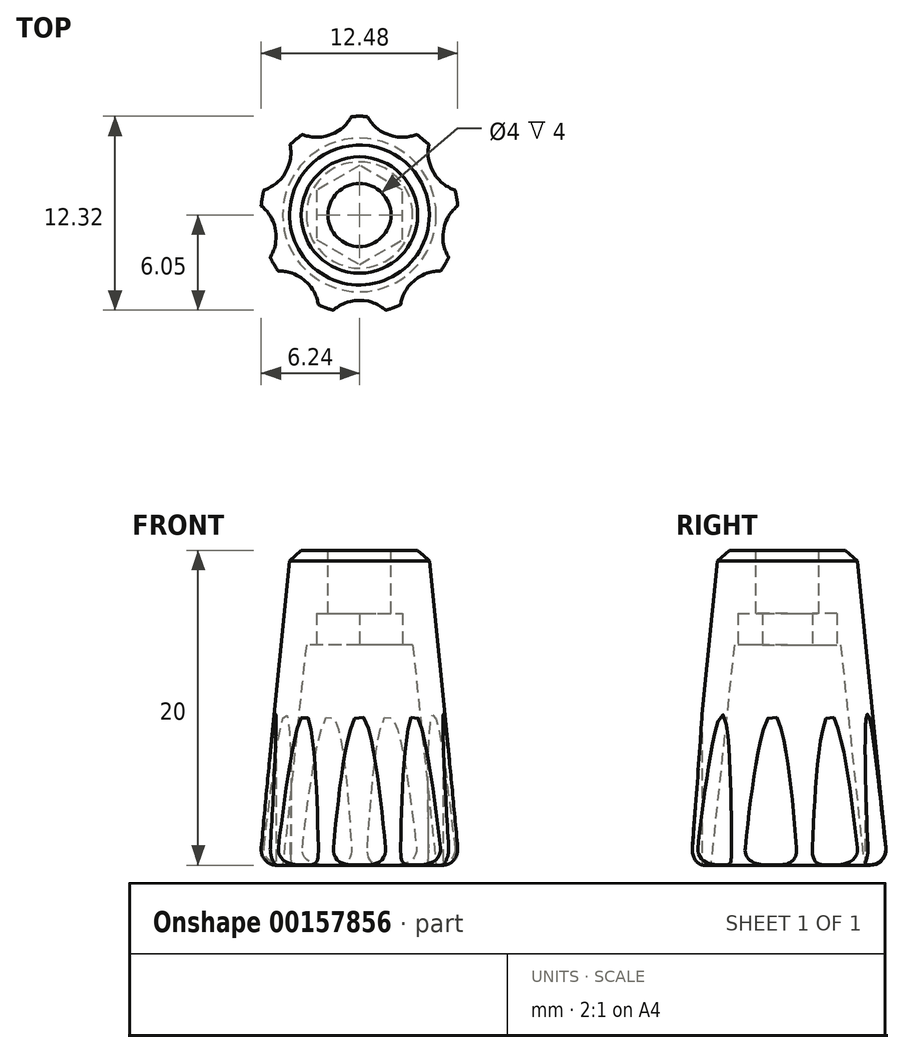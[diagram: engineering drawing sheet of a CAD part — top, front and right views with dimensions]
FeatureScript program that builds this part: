
annotation { "Feature Type Name" : "Feature", "Feature Type Description" : "" }
export const myFeature = defineFeature(function(context is Context, id is Id, definition is map)
    precondition{}
    {
        {
            var Q0;
            Q0=qCreatedBy(makeId("Top.planeOp"),FACE);
            var sketch = newSketch(context, id + "F0", { "sketchPlane" : qUnion([Q0])});
            skCircle(sketch, "E0", {"center": v(0, 0) * mm, "radius": 4.38 * mm});
            skSolve(sketch);
        }
        {
            var Q0;
            Q0=qCreatedBy(makeId("Top.planeOp"),FACE);
            cPlane(context, id + "F1", {"entities" : qUnion([Q0]), "cplaneType" : CPlaneType.OFFSET, "offset" : 20 * mm, "oppositeDirection" : true, "width" : 150 * mm, "height" : 150 * mm});
        }
        {
            var Q0;
            Q0=qCreatedBy(id+"F1.planeOp",FACE);
            var sketch = newSketch(context, id + "F2", { "sketchPlane" : qUnion([Q0])});
            skCircle(sketch, "E1", {"center": v(0, 0) * mm, "radius": 6.38 * mm});
            skSolve(sketch);
        }
        {
            var Q0;
            Q0=makeQuery(id+"F0.imprint","IMPRINT",FACE,{"disambiguationData":[TD([[makeQuery(id+"F0.imprint","IMPRINT",EDGE,{"derivedFrom":sQuery(id+"F0.wireOp",EDGE,"E0")}),1.0]])]});
            var Q1;
            Q1=makeQuery(id+"F2.imprint","IMPRINT",FACE,{"disambiguationData":[TD([[makeQuery(id+"F2.imprint","IMPRINT",EDGE,{"derivedFrom":sQuery(id+"F2.wireOp",EDGE,"E1")}),1.0]])]});
            loft(context, id + "F3", {"sheetProfilesArray" : [{ "sheetProfileEntities" : qUnion([Q0]) }, { "sheetProfileEntities" : qUnion([Q1]) }]});
        }
        {
            var Q0;
            Q0=makeQuery(id+"F3.opLoft","MID_CAP_EDGE",EDGE,{"disambiguationData":[OSD([sQuery(id+"F0.wireOp",EDGE,"E0")])],"capPos":0.0});
            chamfer(context, id + "F4", {"entities" : qUnion([Q0]), "width" : 0.75 * mm, "tangentPropagation" : true});
        }
        {
            var Q0;
            Q0=makeQuery(id+"F3.opLoft","CAP_FACE",FACE,{"disambiguationData":[OSD([makeQuery(id+"F0.imprint","IMPRINT",FACE,{"disambiguationData":[TD([[makeQuery(id+"F0.imprint","IMPRINT",EDGE,{"derivedFrom":sQuery(id+"F0.wireOp",EDGE,"E0")}),1.0]])]})])],"isStart":true});
            var sketch = newSketch(context, id + "F5", { "sketchPlane" : qUnion([Q0])});
            skCircle(sketch, "E2", {"center": v(0, 0) * mm, "radius": 2 * mm});
            skSolve(sketch);
        }
        {
            var Q0;
            Q0 = qSketchRegion(id + "F5", true);
            extrude(context, id + "F6", {"entities" : qUnion([Q0]), "operationType" : NewBodyOperationType.REMOVE, "endBound" : BoundingType.THROUGH_ALL, "oppositeDirection" : true, "depth" : 25 * mm});
        }
        {
            var Q0;
            Q0=makeQuery(id+"F3.opLoft","CAP_FACE",FACE,{"disambiguationData":[OSD([makeQuery(id+"F0.imprint","IMPRINT",FACE,{"disambiguationData":[TD([[makeQuery(id+"F0.imprint","IMPRINT",EDGE,{"derivedFrom":sQuery(id+"F0.wireOp",EDGE,"E0")}),1.0]])]})])],"isStart":true});
            cPlane(context, id + "F7", {"entities" : qUnion([Q0]), "cplaneType" : CPlaneType.OFFSET, "offset" : 6 * mm, "oppositeDirection" : true, "width" : 150 * mm, "height" : 150 * mm});
        }
        {
            var Q0;
            Q0=qCreatedBy(id+"F7.planeOp",FACE);
            var sketch = newSketch(context, id + "F8", { "sketchPlane" : qUnion([Q0])});
            skCircle(sketch, "E3", {"center": v(0, 0) * mm, "radius": 3.38 * mm});
            skSolve(sketch);
        }
        {
            var Q0;
            Q0=makeQuery(id+"F3.opLoft","CAP_FACE",FACE,{"disambiguationData":[OSD([makeQuery(id+"F2.imprint","IMPRINT",FACE,{"disambiguationData":[TD([[makeQuery(id+"F2.imprint","IMPRINT",EDGE,{"derivedFrom":sQuery(id+"F2.wireOp",EDGE,"E1")}),1.0]])]})])],"isStart":true});
            var sketch = newSketch(context, id + "F9", { "sketchPlane" : qUnion([Q0])});
            skCircle(sketch, "E4", {"center": v(0, 0) * mm, "radius": 4.88 * mm});
            skSolve(sketch);
        }
        {
            var Q1;
            Q1 = qSketchRegion(id + "F9", true);
            var Q2;
            Q2 = qSketchRegion(id + "F8", true);
            loft(context, id + "F10", {"operationType" : NewBodyOperationType.REMOVE, "sheetProfilesArray" : [{ "sheetProfileEntities" : qUnion([Q1]) }, { "sheetProfileEntities" : qUnion([Q2]) }]});
        }
        {
            var Q0;
            Q0=makeQuery(id+"F10.boolean.opBoolean","COPY",FACE,{"derivedFrom":makeQuery(id+"F10.opLoft","CAP_FACE",FACE,{"disambiguationData":[OSD([makeQuery(id+"F8.imprint","IMPRINT",FACE,{"disambiguationData":[TD([[makeQuery(id+"F8.imprint","IMPRINT",EDGE,{"derivedFrom":sQuery(id+"F8.wireOp",EDGE,"E3")}),1.0]])]})])],"isStart":true})});
            var sketch = newSketch(context, id + "F11", { "sketchPlane" : qUnion([Q0])});
            skCircle(sketch, "E5.cCircle", {"center": v(0, 0) * mm, "radius": 2.73 * mm, "construction": true});
            skLineSegment(sketch, "E5.0", {"start": v(2.73, 1.57) * mm, "end": v(2.73, -1.57) * mm});
            skLineSegment(sketch, "E5.1", {"start": v(2.73, -1.57) * mm, "end": v(0, -3.15) * mm});
            skLineSegment(sketch, "E5.2", {"start": v(0, -3.15) * mm, "end": v(-2.73, -1.57) * mm});
            skLineSegment(sketch, "E5.3", {"start": v(-2.72, -1.57) * mm, "end": v(-2.73, 1.57) * mm});
            skLineSegment(sketch, "E5.4", {"start": v(-2.73, 1.57) * mm, "end": v(0, 3.15) * mm});
            skLineSegment(sketch, "E5.5", {"start": v(0, 3.15) * mm, "end": v(2.72, 1.57) * mm});
            skPoint(sketch, "E5.0.midPoint", {"position": v(2.73, 0) * mm});
            skSolve(sketch);
        }
        {
            var Q0;
            Q0 = qSketchRegion(id + "F11", true);
            extrude(context, id + "F12", {"entities" : qUnion([Q0]), "operationType" : NewBodyOperationType.REMOVE, "oppositeDirection" : true, "depth" : (2) * mm});
        }
        {
            var Q0;
            Q0=makeQuery(id+"F3.opLoft","CAP_FACE",FACE,{"disambiguationData":[OSD([makeQuery(id+"F2.imprint","IMPRINT",FACE,{"disambiguationData":[TD([[makeQuery(id+"F2.imprint","IMPRINT",EDGE,{"derivedFrom":sQuery(id+"F2.wireOp",EDGE,"E1")}),1.0]])]})])],"isStart":true});
            var sketch = newSketch(context, id + "F13", { "sketchPlane" : qUnion([Q0])});
            skLineSegment(sketch, "E6", {"start": v(0, 0) * mm, "end": v(0, 6.38) * mm});
            skLineSegment(sketch, "E7", {"start": v(-1.75, 6.13) * mm, "end": v(1.75, 6.13) * mm});
            skArc(sketch, "E8", {"start": v(-1.75, 6.13) * mm, "mid": v(0, 5.42) * mm, "end": v(1.75, 6.13) * mm});
            skPoint(sketch, "E8.third.point", {"position": v(0, 5.42) * mm});
            skArc(sketch, "E9.1.0", {"start": v(-5.28, 3.57) * mm, "mid": v(-3.48, 4.15) * mm, "end": v(-2.6, 5.82) * mm});
            skArc(sketch, "E9.2.0", {"start": v(-6.34, -0.66) * mm, "mid": v(-5.33, 0.94) * mm, "end": v(-5.73, 2.79) * mm});
            skArc(sketch, "E9.3.0", {"start": v(-4.43, -4.58) * mm, "mid": v(-4.69, -2.7) * mm, "end": v(-6.18, -1.55) * mm});
            skArc(sketch, "E9.4.0", {"start": v(-0.45, -6.36) * mm, "mid": v(-1.85, -5.09) * mm, "end": v(-3.74, -5.16) * mm});
            skArc(sketch, "E9.5.0", {"start": v(3.74, -5.16) * mm, "mid": v(1.85, -5.09) * mm, "end": v(0.45, -6.36) * mm});
            skArc(sketch, "E9.6.0", {"start": v(6.18, -1.55) * mm, "mid": v(4.69, -2.7) * mm, "end": v(4.43, -4.58) * mm});
            skArc(sketch, "E9.7.0", {"start": v(5.73, 2.79) * mm, "mid": v(5.33, 0.94) * mm, "end": v(6.34, -0.66) * mm});
            skArc(sketch, "E9.8.0", {"start": v(2.6, 5.82) * mm, "mid": v(3.48, 4.15) * mm, "end": v(5.28, 3.57) * mm});
            skPoint(sketch, "E9.center", {"position": v(0, 0) * mm});
            skSolve(sketch);
        }
        {
            var Q0;
            Q0 = qSketchRegion(id + "F13", true);
            var Q1;
            {var subQ0=sQuery(id+"F13.wireOp",EDGE,"E9.8.0");Q1=makeQuery(id+"F13.imprint","IMPRINT",FACE,{"disambiguationData":[TD([[makeQuery(id+"F13.imprint","IMPRINT",EDGE,{"derivedFrom":subQ0}),1.0]])]});}
            var Q2;
            {var subQ0=sQuery(id+"F13.wireOp",EDGE,"E9.7.0");Q2=makeQuery(id+"F13.imprint","IMPRINT",FACE,{"disambiguationData":[TD([[makeQuery(id+"F13.imprint","IMPRINT",EDGE,{"derivedFrom":subQ0}),1.0]])]});}
            var Q3;
            {var subQ0=sQuery(id+"F13.wireOp",EDGE,"E9.6.0");Q3=makeQuery(id+"F13.imprint","IMPRINT",FACE,{"disambiguationData":[TD([[makeQuery(id+"F13.imprint","IMPRINT",EDGE,{"derivedFrom":subQ0}),1.0]])]});}
            var Q4;
            {var subQ0=sQuery(id+"F13.wireOp",EDGE,"E9.5.0");Q4=makeQuery(id+"F13.imprint","IMPRINT",FACE,{"disambiguationData":[TD([[makeQuery(id+"F13.imprint","IMPRINT",EDGE,{"derivedFrom":subQ0}),1.0]])]});}
            var Q5;
            {var subQ0=sQuery(id+"F13.wireOp",EDGE,"E9.4.0");Q5=makeQuery(id+"F13.imprint","IMPRINT",FACE,{"disambiguationData":[TD([[makeQuery(id+"F13.imprint","IMPRINT",EDGE,{"derivedFrom":subQ0}),1.0]])]});}
            var Q6;
            {var subQ0=sQuery(id+"F13.wireOp",EDGE,"E9.3.0");Q6=makeQuery(id+"F13.imprint","IMPRINT",FACE,{"disambiguationData":[TD([[makeQuery(id+"F13.imprint","IMPRINT",EDGE,{"derivedFrom":subQ0}),1.0]])]});}
            var Q7;
            {var subQ0=sQuery(id+"F13.wireOp",EDGE,"E9.2.0");Q7=makeQuery(id+"F13.imprint","IMPRINT",FACE,{"disambiguationData":[TD([[makeQuery(id+"F13.imprint","IMPRINT",EDGE,{"derivedFrom":subQ0}),1.0]])]});}
            var Q8;
            {var subQ0=sQuery(id+"F13.wireOp",EDGE,"E9.1.0");Q8=makeQuery(id+"F13.imprint","IMPRINT",FACE,{"disambiguationData":[TD([[makeQuery(id+"F13.imprint","IMPRINT",EDGE,{"derivedFrom":subQ0}),1.0]])]});}
            var Q9;
            {var subQ0=sQuery(id+"F13.wireOp",EDGE,"E6");var subQ3=sQuery(id+"F13.wireOp",EDGE,"E7");var subQ4=makeQuery(id+"F13.imprint","INTERSECT",VERTEX,{"derivedFrom":[subQ0,subQ3]});Q9=makeQuery(id+"F13.imprint","IMPRINT",FACE,{"disambiguationData":[TD([[makeQuery(id+"F13.imprint","IMPRINT",EDGE,{"disambiguationData":[TD([[subQ4,-1.0]])],"derivedFrom":subQ0}),1.0]])]});}
            var Q10;
            {var subQ0=sQuery(id+"F13.wireOp",EDGE,"E6");var subQ3=sQuery(id+"F13.wireOp",EDGE,"E7");var subQ4=makeQuery(id+"F13.imprint","INTERSECT",VERTEX,{"derivedFrom":[subQ0,subQ3]});Q10=makeQuery(id+"F13.imprint","IMPRINT",FACE,{"disambiguationData":[TD([[makeQuery(id+"F13.imprint","IMPRINT",EDGE,{"disambiguationData":[TD([[subQ4,-1.0]])],"derivedFrom":subQ0}),-1.0]])]});}
            extrude(context, id + "F14", {"entities" : qUnion([Q0, Q1, Q2, Q3, Q4, Q5, Q6, Q7, Q8, Q9, Q10]), "operationType" : NewBodyOperationType.REMOVE, "oppositeDirection" : true, "depth" : 25 * mm});
        }
        {
            var Q0;
            {var subQ0=sQuery(id+"F2.wireOp",EDGE,"E1");var subQ1=sQuery(id+"F0.wireOp",EDGE,"E0");Q0=makeQuery(id+"F14.boolean.opBoolean","SPLIT",EDGE,{"disambiguationData":[TD([makeQuery(id+"F3.opLoft","SWEPT_FACE",FACE,{"disambiguationData":[OSD([subQ1,subQ0])]}),makeQuery(id+"F3.opLoft","CAP_FACE",FACE,{"disambiguationData":[OSD([makeQuery(id+"F2.imprint","IMPRINT",FACE,{"disambiguationData":[TD([[makeQuery(id+"F2.imprint","IMPRINT",EDGE,{"derivedFrom":subQ0}),1.0]])]})])],"isStart":true}),makeQuery(id+"F14.opExtrude","SWEPT_FACE",FACE,{"disambiguationData":[OSD([sQuery(id+"F13.wireOp",EDGE,"E9.1.0")])]}),makeQuery(id+"F14.opExtrude","SWEPT_FACE",FACE,{"disambiguationData":[OSD([sQuery(id+"F13.wireOp",EDGE,"E9.2.0")])]})])],"derivedFrom":makeQuery(id+"F3.opLoft","MID_CAP_EDGE",EDGE,{"disambiguationData":[OSD([subQ1,subQ0])],"capPos":1.0})});}
            fillet(context, id + "F15", {"entities" : qUnion([Q0]), "radius" : 1 * mm, "tangentPropagation" : true, "allowEdgeOverflow" : false});
        }
    });
